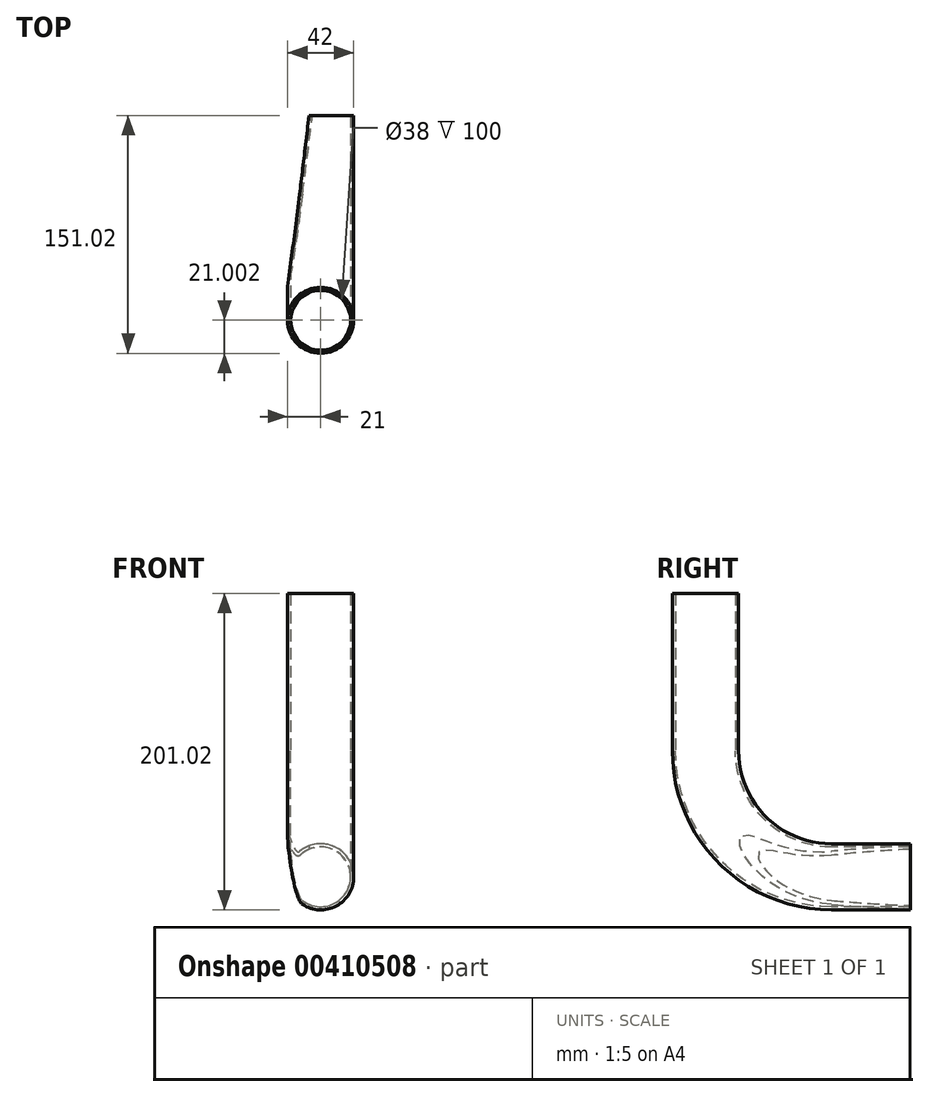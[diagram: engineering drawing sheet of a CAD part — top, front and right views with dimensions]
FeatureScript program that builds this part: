
annotation { "Feature Type Name" : "Feature", "Feature Type Description" : "" }
export const myFeature = defineFeature(function(context is Context, id is Id, definition is map)
    precondition{}
    {
        {
            var Q0;
            Q0=qCreatedBy(makeId("Right.planeOp"),FACE);
            var sketch = newSketch(context, id + "F0", { "sketchPlane" : qUnion([Q0])});
            skArc(sketch, "E0", {"start": v(0, -80) * mm, "mid": v(-56.57, -56.57) * mm, "end": v(-80, 0) * mm});
            skSolve(sketch);
        }
        {
            var Q0;
            Q0=qCreatedBy(makeId("Top.planeOp"),FACE);
            var sketch = newSketch(context, id + "F1", { "sketchPlane" : qUnion([Q0])});
            skCircle(sketch, "E1", {"center": v(0, -80.02) * mm, "radius": 21 * mm});
            skCircle(sketch, "E2", {"center": v(0, -80.02) * mm, "radius": 19 * mm});
            skSolve(sketch);
        }
        {
            var Q0;
            Q0=makeQuery(id+"F1.imprint","IMPRINT",FACE,{"disambiguationData":[TD([[makeQuery(id+"F1.imprint","IMPRINT",EDGE,{"derivedFrom":sQuery(id+"F1.wireOp",EDGE,"E1")}),1.0]])]});
            var Q1;
            Q1=sQuery(id+"F0.wireOp",EDGE,"E0");
            sweep(context, id + "F2", {"profiles" : qUnion([Q0]), "path" : qUnion([Q1])});
        }
        {
            var Q0;
            Q0=makeQuery(id+"F2.opSweep","CAP_FACE",FACE,{"disambiguationData":[OSD([sQuery(id+"F0.wireOp",VERTEX,"E0.end"),sQuery(id+"F1.wireOp",EDGE,"E1"),sQuery(id+"F1.wireOp",EDGE,"E2")])],"isStart":true});
            extrude(context, id + "F3", {"entities" : qUnion([Q0]), "operationType" : NewBodyOperationType.ADD, "depth" : 100 * mm});
        }
        {
            var Q0;
            Q0=makeQuery(id+"F2.opSweep","CAP_FACE",FACE,{"disambiguationData":[OSD([sQuery(id+"F0.wireOp",VERTEX,"E0.start"),sQuery(id+"F1.wireOp",EDGE,"E1"),sQuery(id+"F1.wireOp",EDGE,"E2")])],"isStart":false});
            extrude(context, id + "F4", {"entities" : qUnion([Q0]), "operationType" : NewBodyOperationType.ADD, "depth" : 50 * mm});
        }
        {
            var Q0;
            Q0=makeQuery(id+"F4.opExtrude","SWEPT_FACE",FACE,{"disambiguationData":[OSD([sQuery(id+"F0.wireOp",VERTEX,"E0.start"),sQuery(id+"F1.wireOp",EDGE,"E2")])]});
            cPlane(context, id + "F5", {"entities" : qUnion([Q0]), "cplaneType" : CPlaneType.LINE_ANGLE, "offset" : 25 * mm, "angle" : 357 * degree, "width" : 150 * mm, "height" : 150 * mm});
        }
        {
            var Q0;
            Q0=qCreatedBy(id+"F5.planeOp",FACE);
            var sketch = newSketch(context, id + "F6", { "sketchPlane" : qUnion([Q0])});
            skLineSegment(sketch, "E3", {"start": v(-10.52, 50) * mm, "end": v(-35.08, -150) * mm});
            skLineSegment(sketch, "E4", {"start": v(-35.08, -150) * mm, "end": v(-50, -150) * mm});
            skLineSegment(sketch, "E5", {"start": v(-50, -150) * mm, "end": v(-50, 50) * mm});
            skLineSegment(sketch, "E6", {"start": v(-50, 50) * mm, "end": v(-10.52, 50) * mm});
            skLineSegment(sketch, "E7.0", {"start": v(14.81, 50) * mm, "end": v(-23.19, 50) * mm});
            skSolve(sketch);
        }
        {
            var Q0;
            Q0 = qSketchRegion(id + "F6", true);
            extrude(context, id + "F7", {"entities" : qUnion([Q0]), "operationType" : NewBodyOperationType.REMOVE, "depth" : 200 * mm, "symmetric" : true});
        }
    });
